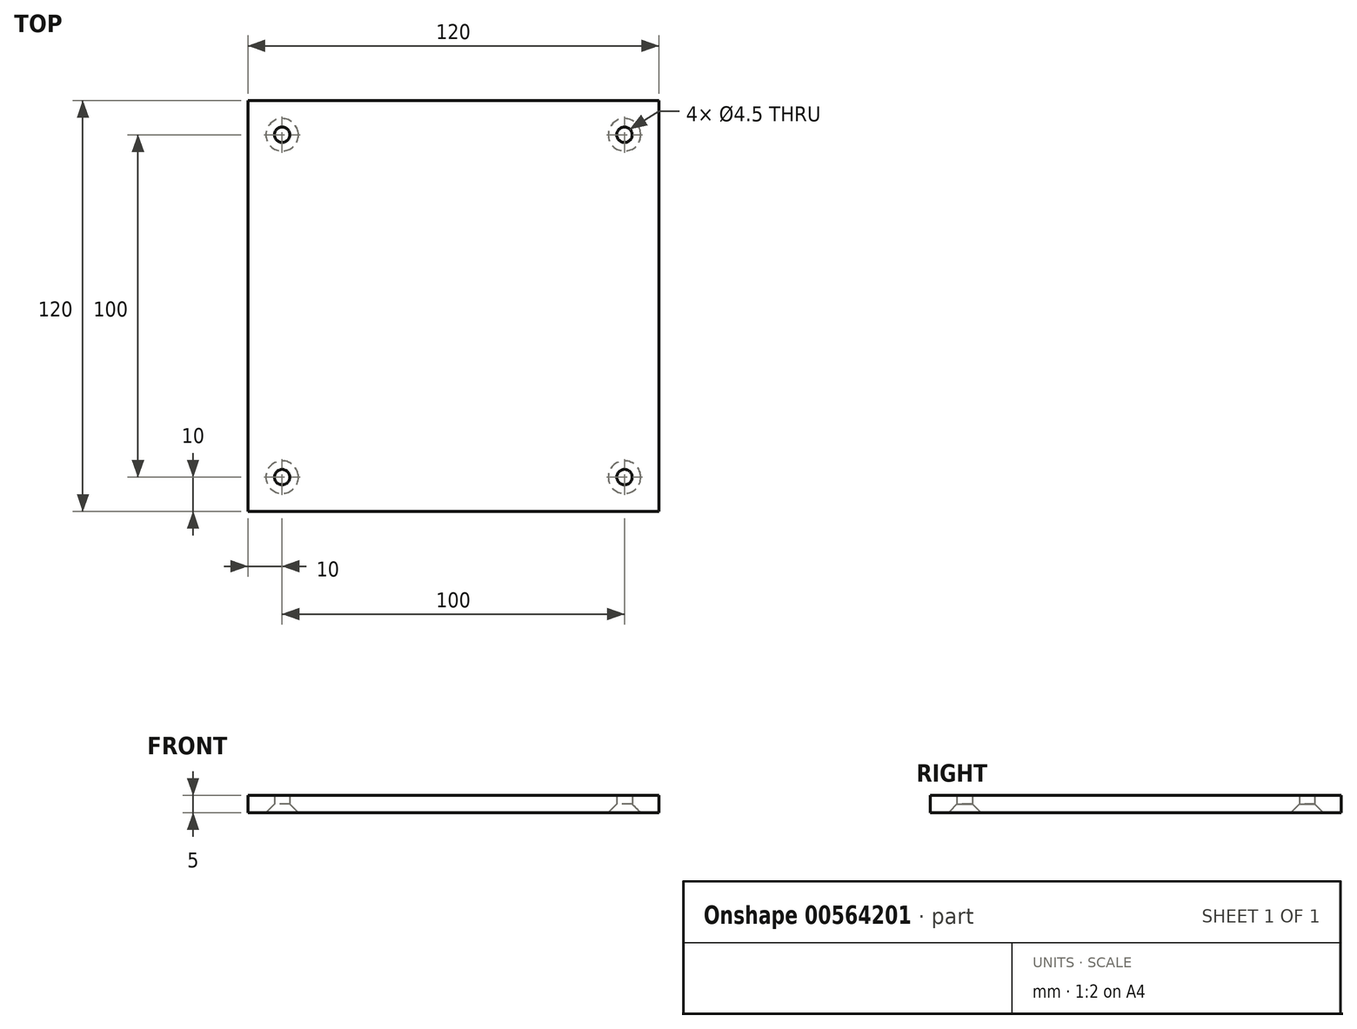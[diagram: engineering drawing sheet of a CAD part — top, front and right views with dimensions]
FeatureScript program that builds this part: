
annotation { "Feature Type Name" : "Feature", "Feature Type Description" : "" }
export const myFeature = defineFeature(function(context is Context, id is Id, definition is map)
    precondition{}
    {
        {
            var Q0;
            Q0=qCreatedBy(makeId("Top.planeOp"),FACE);
            var sketch = newSketch(context, id + "F0", { "sketchPlane" : qUnion([Q0])});
            skLineSegment(sketch, "E0.bottom", {"start": v(-60, 60) * mm, "end": v(60, 60) * mm});
            skLineSegment(sketch, "E0.top", {"start": v(-60, -60) * mm, "end": v(60, -60) * mm});
            skLineSegment(sketch, "E0.left", {"start": v(-60, 60) * mm, "end": v(-60, -60) * mm});
            skLineSegment(sketch, "E0.right", {"start": v(60, 60) * mm, "end": v(60, -60) * mm});
            skLineSegment(sketch, "E1", {"start": v(-70, 50) * mm, "end": v(70, 50) * mm, "construction": true});
            skLineSegment(sketch, "E2", {"start": v(50, 70) * mm, "end": v(50, -70) * mm, "construction": true});
            skLineSegment(sketch, "E3", {"start": v(-50, 70) * mm, "end": v(-50, -70) * mm, "construction": true});
            skLineSegment(sketch, "E4", {"start": v(-70, -50) * mm, "end": v(70, -50) * mm, "construction": true});
            skCircle(sketch, "E5", {"center": v(-50, 50) * mm, "radius": 2.25 * mm});
            skCircle(sketch, "E6", {"center": v(50, 50) * mm, "radius": 2.25 * mm});
            skCircle(sketch, "E7", {"center": v(50, -50) * mm, "radius": 2.25 * mm});
            skCircle(sketch, "E8", {"center": v(-50, -50) * mm, "radius": 2.25 * mm});
            skSolve(sketch);
        }
        {
            var Q0;
            Q0 = qSketchRegion(id + "F0", true);
            extrude(context, id + "F1", {"entities" : qUnion([Q0]), "depth" : 5 * mm, "offsetDistance" : 25 * mm});
        }
        {
            var Q0;
            Q0=makeQuery(id+"F1.opExtrude","CAP_EDGE",EDGE,{"disambiguationData":[OSD([sQuery(id+"F0.wireOp",EDGE,"E7")])],"isStart":true});
            var Q1;
            Q1=makeQuery(id+"F1.opExtrude","CAP_EDGE",EDGE,{"disambiguationData":[OSD([sQuery(id+"F0.wireOp",EDGE,"E8")])],"isStart":true});
            var Q2;
            Q2=makeQuery(id+"F1.opExtrude","CAP_EDGE",EDGE,{"disambiguationData":[OSD([sQuery(id+"F0.wireOp",EDGE,"E5")])],"isStart":true});
            var Q3;
            Q3=makeQuery(id+"F1.opExtrude","CAP_EDGE",EDGE,{"disambiguationData":[OSD([sQuery(id+"F0.wireOp",EDGE,"E6")])],"isStart":true});
            chamfer(context, id + "F2", {"entities" : qUnion([Q0, Q1, Q2, Q3]), "width" : 2.5 * mm});
        }
    });
